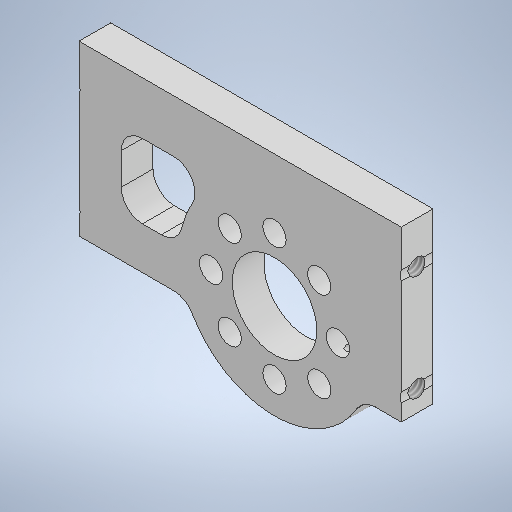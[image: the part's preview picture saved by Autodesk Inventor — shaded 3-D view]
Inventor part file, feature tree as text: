
AUTODESK INVENTOR PART (.ipt)
format: ipt  version: 2025.1 (Build 291241000, 241)  size: 388,608 bytes
history: native  units: mm
features: sketch x6, extrude x4, other x2, hole x2, fillet x2, projected_geometry x1
ambient origin geometry x8: Origin, YZ Plane, XZ Plane, XY Plane, X Axis, Y Axis, Z Axis, Center Point
bodies: Body1 (feature_tree)
feature tree (17):
  other  "ソリッド1"
  extrude  "押し出し1"  Depth=30.5mm
  extrude  "押し出し2"  Depth=25.0mm
  hole  "穴2"  [1 undecoded]
  hole  "穴3"  [1 undecoded]
  extrude  "押し出し3"  Depth=2.2mm
  extrude  "押し出し4"  Depth=3.0mm TaperAngle=0.0deg
  fillet  "フィレット1"  Radius=8.0mm
  fillet  "フィレット2"  Radius=12.0mm
  sketch  "スケッチ1"
  sketch  "スケッチ3"
  other  "スケッチ円形状パターン1"
  sketch  "スケッチ4"
  sketch  "スケッチ5"
  sketch  "スケッチ6"
  sketch  "スケッチ7"
  projected_geometry  "投影ループ1"
note: 2 required parameter values undecoded (feature->parameter linkage not recoverable at this tier; creation-order binding heuristic only, values carry confidence <= 0.55)
